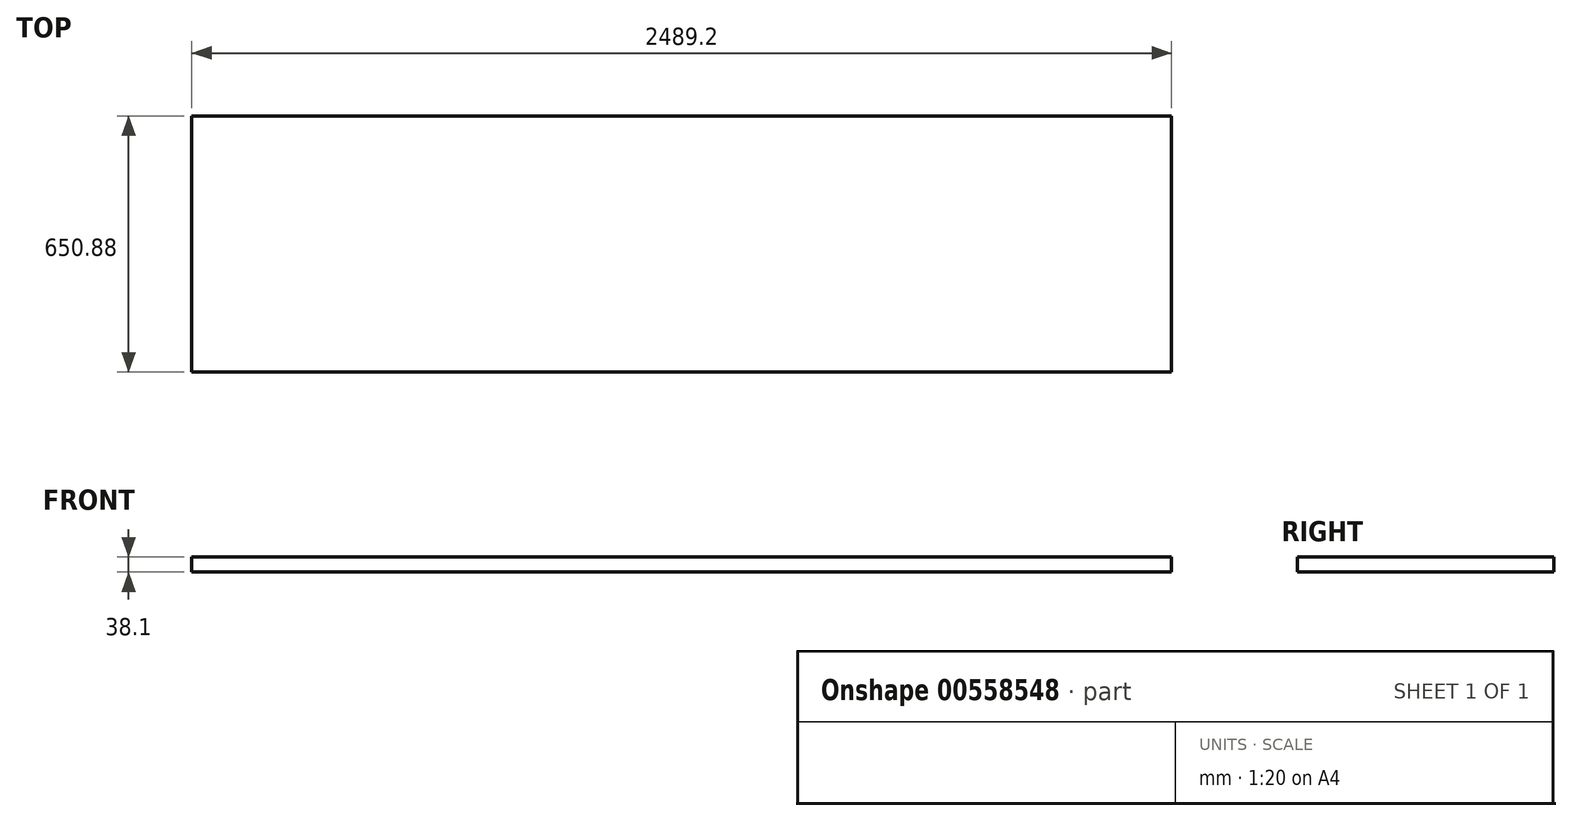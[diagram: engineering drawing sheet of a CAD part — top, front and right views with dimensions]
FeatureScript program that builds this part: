
annotation { "Feature Type Name" : "Feature", "Feature Type Description" : "" }
export const myFeature = defineFeature(function(context is Context, id is Id, definition is map)
    precondition{}
    {
        {
            var Q0;
            Q0=qCreatedBy(makeId("Top.planeOp"),FACE);
            var sketch = newSketch(context, id + "F0", { "sketchPlane" : qUnion([Q0])});
            skLineSegment(sketch, "E0.bottom", {"start": v(-2407.4, 611.97) * mm, "end": v(81.8, 611.97) * mm});
            skLineSegment(sketch, "E0.top", {"start": v(-2407.4, -38.9) * mm, "end": v(81.8, -38.9) * mm});
            skLineSegment(sketch, "E0.left", {"start": v(-2407.4, 611.97) * mm, "end": v(-2407.4, -38.9) * mm});
            skLineSegment(sketch, "E0.right", {"start": v(81.8, 611.97) * mm, "end": v(81.8, -38.9) * mm});
            skSolve(sketch);
        }
        {
            var Q0;
            Q0=makeQuery(id+"F0.imprint","IMPRINT",FACE,{"disambiguationData":[TD([[makeQuery(id+"F0.imprint","IMPRINT",EDGE,{"derivedFrom":sQuery(id+"F0.wireOp",EDGE,"E0.bottom")}),-1.0]])]});
            extrude(context, id + "F1", {"entities" : qUnion([Q0]), "depth" : 38.1 * mm, "offsetDistance" : 25.4 * mm});
        }
    });
